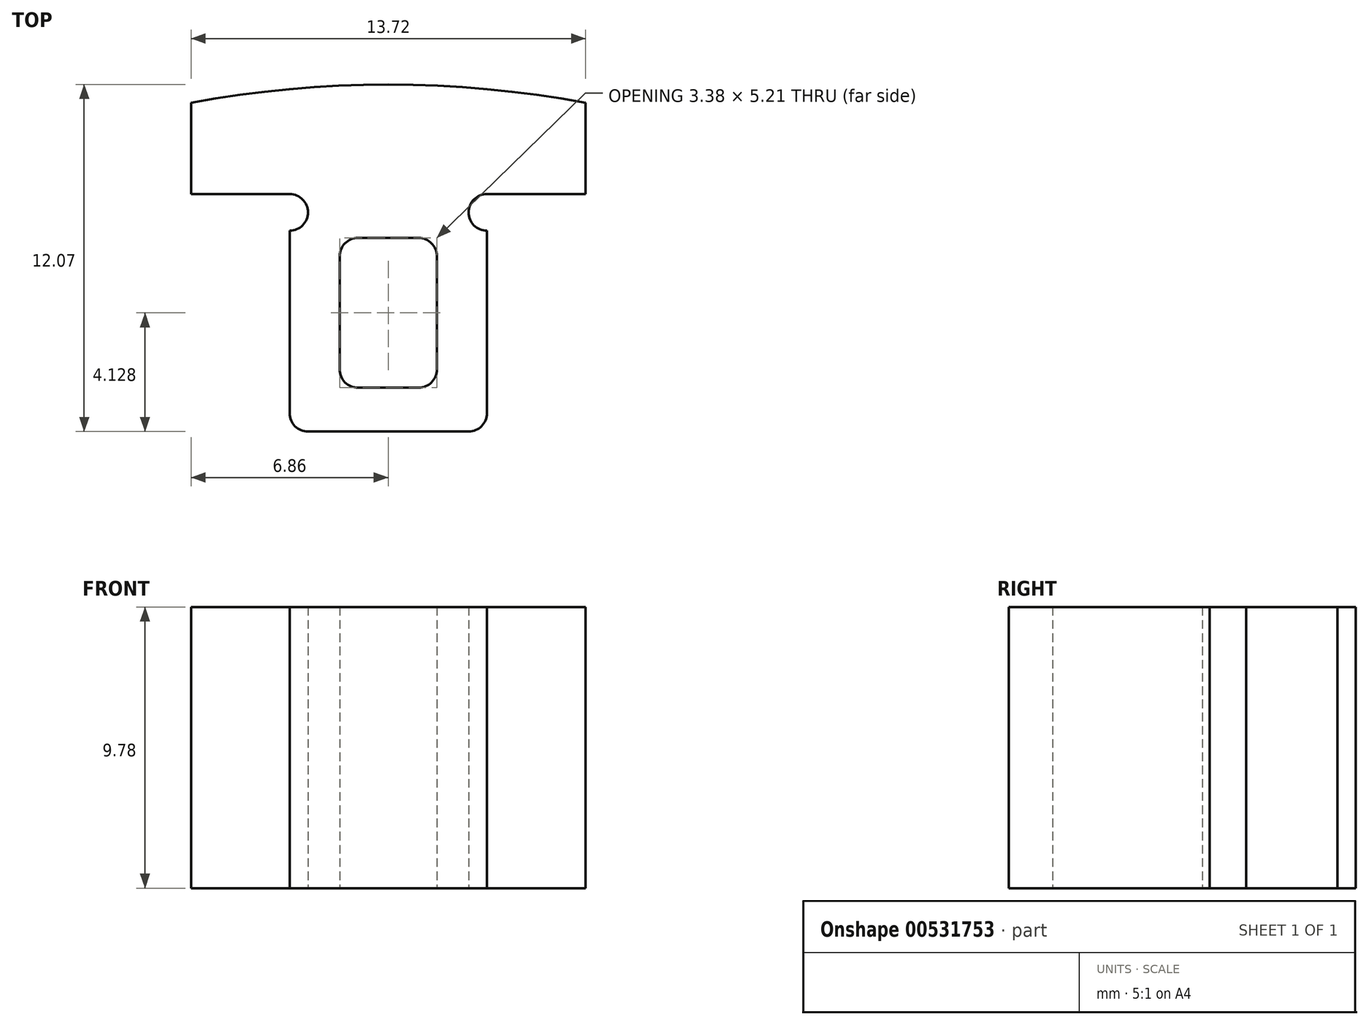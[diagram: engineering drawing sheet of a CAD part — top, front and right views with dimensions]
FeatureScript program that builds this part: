
annotation { "Feature Type Name" : "Feature", "Feature Type Description" : "" }
export const myFeature = defineFeature(function(context is Context, id is Id, definition is map)
    precondition{}
    {
        {
            var Q0;
            Q0=qCreatedBy(makeId("Top.planeOp"),FACE);
            var sketch = newSketch(context, id + "F0", { "sketchPlane" : qUnion([Q0])});
            skLineSegment(sketch, "E0.bottom", {"start": v(-2.8, 0) * mm, "end": v(2.8, 0) * mm});
            skLineSegment(sketch, "E0.left", {"start": v(3.43, 0.64) * mm, "end": v(3.43, 6.99) * mm});
            skLineSegment(sketch, "E0.right", {"start": v(-3.43, 0.64) * mm, "end": v(-3.43, 6.99) * mm});
            skPoint(sketch, "E1.oppositeSnap0", {"position": v(0, 8.26) * mm});
            skLineSegment(sketch, "E1.top", {"start": v(-6.86, 8.26) * mm, "end": v(-3.43, 8.26) * mm});
            skLineSegment(sketch, "E1.left", {"start": v(-6.86, 11.43) * mm, "end": v(-6.86, 8.26) * mm});
            skLineSegment(sketch, "E1.right", {"start": v(6.86, 11.43) * mm, "end": v(6.86, 8.26) * mm});
            skLineSegment(sketch, "E2", {"start": v(0, 0) * mm, "end": v(0, 11.43) * mm, "construction": true});
            skLineSegment(sketch, "E3.bottom", {"start": v(-1.05, 6.73) * mm, "end": v(1.05, 6.73) * mm});
            skLineSegment(sketch, "E3.top", {"start": v(-1.05, 1.52) * mm, "end": v(1.05, 1.52) * mm});
            skLineSegment(sketch, "E3.left", {"start": v(-1.69, 6.1) * mm, "end": v(-1.69, 2.16) * mm});
            skLineSegment(sketch, "E3.right", {"start": v(1.69, 6.1) * mm, "end": v(1.69, 2.16) * mm});
            skLineSegment(sketch, "E4", {"start": v(-3.43, 4.13) * mm, "end": v(3.43, 4.13) * mm, "construction": true});
            skArc(sketch, "E5", {"start": v(-3.43, 6.99) * mm, "mid": v(-2.8, 7.62) * mm, "end": v(-3.43, 8.26) * mm});
            skArc(sketch, "E6", {"start": v(3.43, 8.26) * mm, "mid": v(2.8, 7.62) * mm, "end": v(3.43, 6.99) * mm});
            skLineSegment(sketch, "E7.trimOffspring", {"start": v(3.43, 8.26) * mm, "end": v(6.86, 8.26) * mm});
            skArc(sketch, "E8", {"start": v(-6.86, 11.43) * mm, "mid": v(0, 12.07) * mm, "end": v(6.86, 11.43) * mm});
            skLineSegment(sketch, "E9", {"start": v(0, 11.43) * mm, "end": v(0, 12.07) * mm, "construction": true});
            skPoint(sketch, "E10.visualSharp", {"position": v(-1.69, 6.73) * mm});
            skArc(sketch, "E10.filletArc", {"start": v(-1.05, 6.73) * mm, "mid": v(-1.5, 6.55) * mm, "end": v(-1.69, 6.1) * mm});
            skPoint(sketch, "E11.visualSharp", {"position": v(1.69, 6.73) * mm});
            skArc(sketch, "E11.filletArc", {"start": v(1.69, 6.1) * mm, "mid": v(1.5, 6.55) * mm, "end": v(1.05, 6.73) * mm});
            skPoint(sketch, "E12.visualSharp", {"position": v(1.69, 1.52) * mm});
            skArc(sketch, "E12.filletArc", {"start": v(1.05, 1.52) * mm, "mid": v(1.5, 1.7) * mm, "end": v(1.69, 2.16) * mm});
            skPoint(sketch, "E13.visualSharp", {"position": v(-1.69, 1.52) * mm});
            skArc(sketch, "E13.filletArc", {"start": v(-1.69, 2.16) * mm, "mid": v(-1.5, 1.7) * mm, "end": v(-1.05, 1.52) * mm});
            skPoint(sketch, "E14.visualSharp", {"position": v(3.43, 0) * mm});
            skArc(sketch, "E14.filletArc", {"start": v(2.8, 0) * mm, "mid": v(3.24, 0.19) * mm, "end": v(3.43, 0.64) * mm});
            skPoint(sketch, "E15.visualSharp", {"position": v(-3.43, 0) * mm});
            skArc(sketch, "E15.filletArc", {"start": v(-3.43, 0.64) * mm, "mid": v(-3.24, 0.19) * mm, "end": v(-2.8, 0) * mm});
            skSolve(sketch);
        }
        {
            var Q0;
            Q0 = qSketchRegion(id + "F0", true);
            extrude(context, id + "F1", {"entities" : qUnion([Q0]), "depth" : 9.78 * mm, "offsetDistance" : 25.4 * mm});
        }
    });
